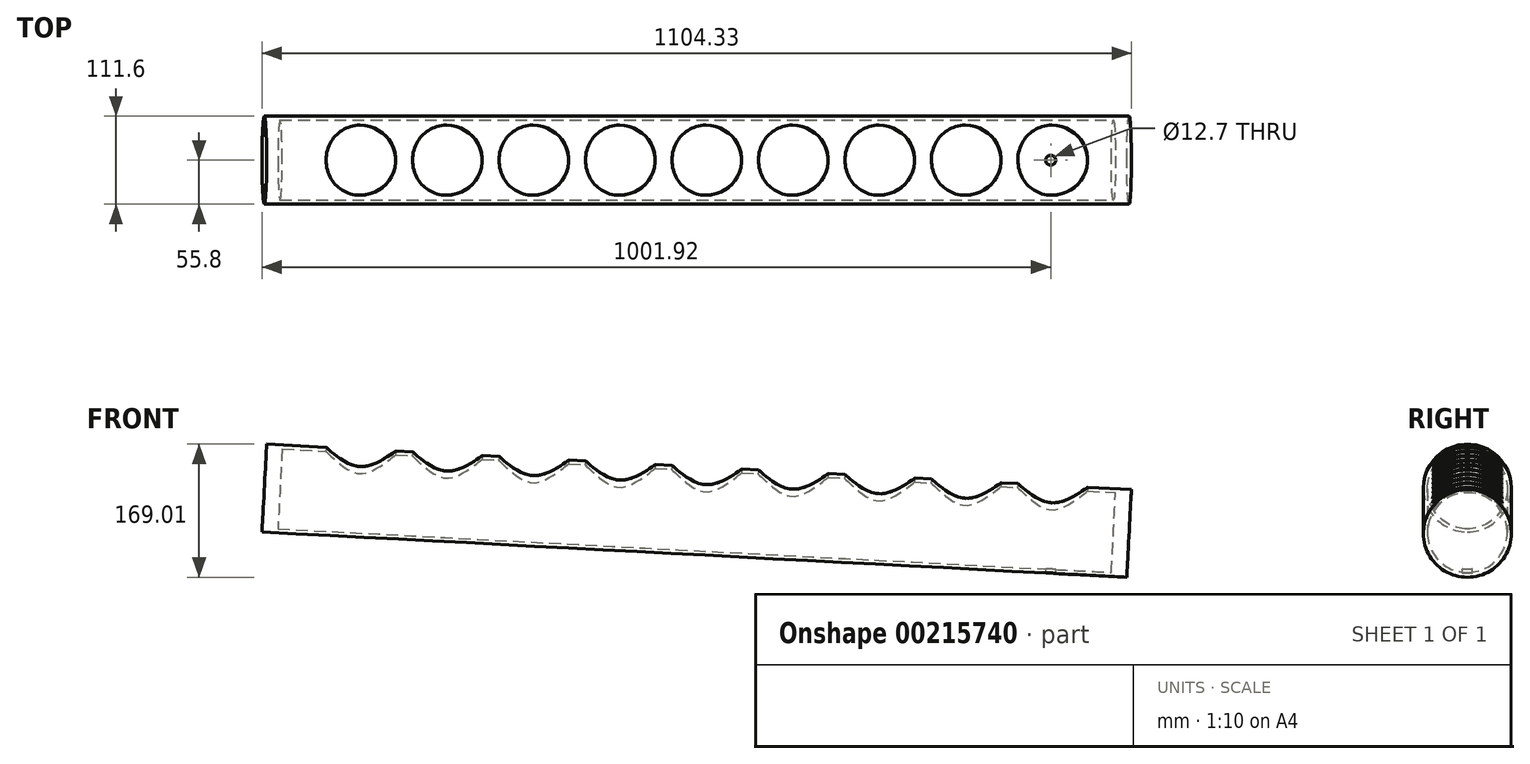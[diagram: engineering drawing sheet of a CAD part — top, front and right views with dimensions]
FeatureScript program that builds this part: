
annotation { "Feature Type Name" : "Feature", "Feature Type Description" : "" }
export const myFeature = defineFeature(function(context is Context, id is Id, definition is map)
    precondition{}
    {
        {
            var Q0;
            Q0=qCreatedBy(makeId("Right.planeOp"),FACE);
            var sketch = newSketch(context, id + "F0", { "sketchPlane" : qUnion([Q0])});
            skCircle(sketch, "E0", {"center": v(0, 0) * mm, "radius": 50.8 * mm});
            skCircle(sketch, "E1.0", {"center": v(0, 0) * mm, "radius": 55.8 * mm});
            skLineSegment(sketch, "E2", {"start": v(-50.8, 0) * mm, "end": v(50.8, 0) * mm, "construction": true});
            skSolve(sketch);
        }
        {
            var Q0;
            Q0 = qSketchRegion(id + "F0", true);
            extrude(context, id + "F1", {"entities" : qUnion([Q0]), "oppositeDirection" : true, "depth" : 1100 * mm});
        }
        {
            var Q0;
            Q0=qCreatedBy(makeId("Right.planeOp"),FACE);
            var sketch = newSketch(context, id + "F2", { "sketchPlane" : qUnion([Q0])});
            skLineSegment(sketch, "E3", {"start": v(-70.21, 0) * mm, "end": v(69.9, 0) * mm, "construction": true});
            skSolve(sketch);
        }
        {
            var Q0;
            Q0=qCreatedBy(makeId("Top.planeOp"),FACE);
            var sketch = newSketch(context, id + "F3", { "sketchPlane" : qUnion([Q0])});
            skCircle(sketch, "E4", {"center": v(-100, 0) * mm, "radius": 44.45 * mm});
            skCircle(sketch, "E5.1.0.0", {"center": v(-210, 0) * mm, "radius": 44.45 * mm});
            skCircle(sketch, "E5.2.0.0", {"center": v(-320, 0) * mm, "radius": 44.45 * mm});
            skCircle(sketch, "E5.3.0.0", {"center": v(-430, 0) * mm, "radius": 44.45 * mm});
            skCircle(sketch, "E5.4.0.0", {"center": v(-540, 0) * mm, "radius": 44.45 * mm});
            skCircle(sketch, "E5.5.0.0", {"center": v(-650, 0) * mm, "radius": 44.45 * mm});
            skCircle(sketch, "E5.6.0.0", {"center": v(-760, 0) * mm, "radius": 44.45 * mm});
            skCircle(sketch, "E5.7.0.0", {"center": v(-870, 0) * mm, "radius": 44.45 * mm});
            skCircle(sketch, "E5.8.0.0", {"center": v(-980, 0) * mm, "radius": 44.45 * mm});
            skLineSegment(sketch, "E5.direction1", {"start": v(-100, 0) * mm, "end": v(-210, 0) * mm, "construction": true});
            skSolve(sketch);
        }
        {
            var Q0;
            Q0 = qSketchRegion(id + "F3", true);
            extrude(context, id + "F4", {"entities" : qUnion([Q0]), "operationType" : NewBodyOperationType.REMOVE, "endBound" : BoundingType.THROUGH_ALL, "depth" : 25 * mm});
        }
        {
            var Q0;
            Q0=makeQuery(id+"F1.opExtrude","SWEPT_BODY",BODY,{"disambiguationData":[OSD([sQuery(id+"F0.wireOp",EDGE,"E0"),sQuery(id+"F0.wireOp",EDGE,"E1.0")])]});
            var Q1;
            Q1=sQuery(id+"F2.wireOp",EDGE,"E3");
            transform(context, id + "F5", {"entities" : qUnion([Q0]), "transformType" : TransformType.ROTATION, "transformAxis" : qUnion([Q1]), "angle" : 3 * degree, "makeCopy" : false});
        }
        {
            var Q0;
            Q0=makeQuery(id+"F1.opExtrude","CAP_FACE",FACE,{"disambiguationData":[OSD([sQuery(id+"F0.wireOp",EDGE,"E0"),sQuery(id+"F0.wireOp",EDGE,"E1.0")])],"isStart":true});
            var sketch = newSketch(context, id + "F6", { "sketchPlane" : qUnion([Q0])});
            skCircle(sketch, "E6", {"center": v(0, 0) * mm, "radius": 50.8 * mm});
            skSolve(sketch);
        }
        {
            var Q0;
            Q0 = qSketchRegion(id + "F6", true);
            extrude(context, id + "F7", {"entities" : qUnion([Q0]), "operationType" : NewBodyOperationType.ADD, "oppositeDirection" : true, "depth" : 20 * mm});
        }
        {
            var Q0;
            Q0=makeQuery(id+"F1.opExtrude","CAP_FACE",FACE,{"disambiguationData":[OSD([sQuery(id+"F0.wireOp",EDGE,"E0"),sQuery(id+"F0.wireOp",EDGE,"E1.0")])],"isStart":false});
            var sketch = newSketch(context, id + "F8", { "sketchPlane" : qUnion([Q0])});
            skCircle(sketch, "E7", {"center": v(0, 0) * mm, "radius": 53.17 * mm});
            skSolve(sketch);
        }
        {
            var Q0;
            Q0 = qSketchRegion(id + "F8", true);
            extrude(context, id + "F9", {"entities" : qUnion([Q0]), "operationType" : NewBodyOperationType.ADD, "oppositeDirection" : true, "depth" : 20 * mm});
        }
        {
            var Q0;
            Q0=qCreatedBy(makeId("Top.planeOp"),FACE);
            var sketch = newSketch(context, id + "F10", { "sketchPlane" : qUnion([Q0])});
            skCircle(sketch, "E8", {"center": v(-99.5, 0) * mm, "radius": 6.35 * mm});
            skSolve(sketch);
        }
        {
            var Q0;
            Q0 = qSketchRegion(id + "F10", true);
            extrude(context, id + "F11", {"entities" : qUnion([Q0]), "operationType" : NewBodyOperationType.REMOVE, "endBound" : BoundingType.THROUGH_ALL, "oppositeDirection" : true, "depth" : 25 * mm});
        }
    });
